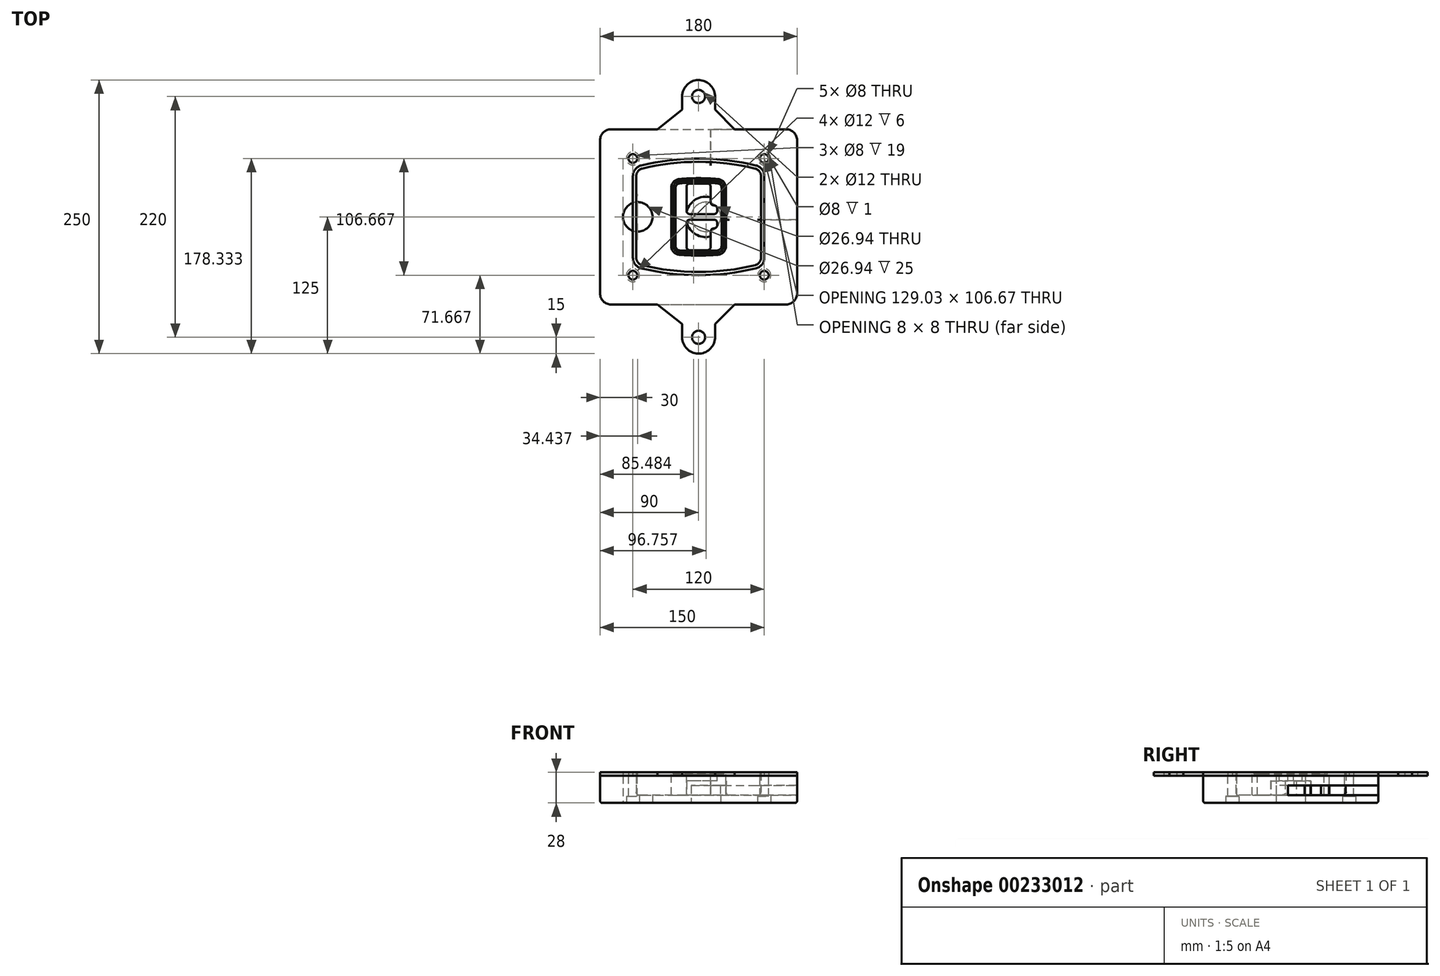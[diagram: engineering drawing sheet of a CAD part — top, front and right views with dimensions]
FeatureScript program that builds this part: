
annotation { "Feature Type Name" : "Feature", "Feature Type Description" : "" }
export const myFeature = defineFeature(function(context is Context, id is Id, definition is map)
    precondition{}
    {
        {
            var Q0;
            Q0=qCreatedBy(makeId("Top.planeOp"),FACE);
            var sketch = newSketch(context, id + "F0", { "sketchPlane" : qUnion([Q0])});
            skPoint(sketch, "E0.rect.middle", {"position": v(0, 0) * mm});
            skLineSegment(sketch, "E1.bottom", {"start": v(-80, -80) * mm, "end": v(80, -80) * mm});
            skLineSegment(sketch, "E1.top", {"start": v(-80, 80) * mm, "end": v(80, 80) * mm});
            skLineSegment(sketch, "E1.left", {"start": v(-90, -70) * mm, "end": v(-90, 70) * mm});
            skLineSegment(sketch, "E1.right", {"start": v(90, -70) * mm, "end": v(90, 70) * mm});
            skLineSegment(sketch, "E2", {"start": v(-90, 80) * mm, "end": v(90, -80) * mm, "construction": true});
            skLineSegment(sketch, "E3", {"start": v(90, 80) * mm, "end": v(-90, -80) * mm, "construction": true});
            skCircle(sketch, "E4", {"center": v(-60, 53.33) * mm, "radius": 4 * mm});
            skCircle(sketch, "E5", {"center": v(60, 53.33) * mm, "radius": 4 * mm});
            skCircle(sketch, "E6", {"center": v(60, -53.33) * mm, "radius": 4 * mm});
            skCircle(sketch, "E7", {"center": v(-60, -53.33) * mm, "radius": 4 * mm});
            skLineSegment(sketch, "E8", {"start": v(-60, 53.33) * mm, "end": v(60, 53.33) * mm, "construction": true});
            skLineSegment(sketch, "E9", {"start": v(60, 53.33) * mm, "end": v(60, -53.33) * mm, "construction": true});
            skLineSegment(sketch, "E10", {"start": v(60, -53.33) * mm, "end": v(-60, -53.33) * mm, "construction": true});
            skLineSegment(sketch, "E11", {"start": v(-60, -53.33) * mm, "end": v(-60, 53.33) * mm, "construction": true});
            skLineSegment(sketch, "E12", {"start": v(-60, 37.3) * mm, "end": v(-60, -37.3) * mm});
            skLineSegment(sketch, "E13", {"start": v(60, 37.3) * mm, "end": v(60, -37.3) * mm});
            skArc(sketch, "E14", {"start": v(52.38, 47.01) * mm, "mid": v(0, 53.33) * mm, "end": v(-52.38, 47.01) * mm});
            skArc(sketch, "E15", {"start": v(-52.38, -47.01) * mm, "mid": v(0, -53.33) * mm, "end": v(52.38, -47.01) * mm});
            skLineSegment(sketch, "E16", {"start": v(-60, 0) * mm, "end": v(60, 0) * mm, "construction": true});
            skPoint(sketch, "E17.visualSharp", {"position": v(-60, -45) * mm});
            skArc(sketch, "E17.filletArc", {"start": v(-60, -37.3) * mm, "mid": v(-57.87, -43.47) * mm, "end": v(-52.38, -47.01) * mm});
            skPoint(sketch, "E18.visualSharp", {"position": v(-60, 45) * mm});
            skArc(sketch, "E18.filletArc", {"start": v(-52.38, 47.01) * mm, "mid": v(-57.87, 43.47) * mm, "end": v(-60, 37.3) * mm});
            skPoint(sketch, "E19.visualSharp", {"position": v(60, 45) * mm});
            skArc(sketch, "E19.filletArc", {"start": v(60, 37.3) * mm, "mid": v(57.87, 43.47) * mm, "end": v(52.38, 47.01) * mm});
            skPoint(sketch, "E20.visualSharp", {"position": v(60, -45) * mm});
            skArc(sketch, "E20.filletArc", {"start": v(52.38, -47.01) * mm, "mid": v(57.87, -43.47) * mm, "end": v(60, -37.3) * mm});
            skPoint(sketch, "E21.visualSharp", {"position": v(-90, 80) * mm});
            skArc(sketch, "E21.filletArc", {"start": v(-80, 80) * mm, "mid": v(-87.07, 77.07) * mm, "end": v(-90, 70) * mm});
            skPoint(sketch, "E22.visualSharp", {"position": v(90, 80) * mm});
            skArc(sketch, "E22.filletArc", {"start": v(90, 70) * mm, "mid": v(87.07, 77.07) * mm, "end": v(80, 80) * mm});
            skPoint(sketch, "E23.visualSharp", {"position": v(90, -80) * mm});
            skArc(sketch, "E23.filletArc", {"start": v(80, -80) * mm, "mid": v(87.07, -77.07) * mm, "end": v(90, -70) * mm});
            skPoint(sketch, "E24.visualSharp", {"position": v(-90, -80) * mm});
            skArc(sketch, "E24.filletArc", {"start": v(-90, -70) * mm, "mid": v(-87.07, -77.07) * mm, "end": v(-80, -80) * mm});
            skArc(sketch, "E25.0", {"start": v(57, 37.3) * mm, "mid": v(55.5, 41.62) * mm, "end": v(51.67, 44.1) * mm});
            skLineSegment(sketch, "E25.1", {"start": v(57, 37.3) * mm, "end": v(57, -37.3) * mm});
            skArc(sketch, "E25.2", {"start": v(51.67, -44.1) * mm, "mid": v(55.5, -41.62) * mm, "end": v(57, -37.3) * mm});
            skArc(sketch, "E25.3", {"start": v(-51.67, -44.1) * mm, "mid": v(0, -50.33) * mm, "end": v(51.67, -44.1) * mm});
            skArc(sketch, "E25.4", {"start": v(-57, -37.3) * mm, "mid": v(-55.5, -41.62) * mm, "end": v(-51.67, -44.1) * mm});
            skArc(sketch, "E25.5", {"start": v(51.67, 44.1) * mm, "mid": v(0, 50.33) * mm, "end": v(-51.67, 44.1) * mm});
            skLineSegment(sketch, "E25.6", {"start": v(-57, 37.3) * mm, "end": v(-57, -37.3) * mm});
            skArc(sketch, "E25.7", {"start": v(-51.67, 44.1) * mm, "mid": v(-55.5, 41.62) * mm, "end": v(-57, 37.3) * mm});
            skArc(sketch, "E26.0", {"start": v(-53.33, 50.9) * mm, "mid": v(-61.01, 45.94) * mm, "end": v(-64, 37.3) * mm});
            skArc(sketch, "E26.1", {"start": v(53.33, 50.9) * mm, "mid": v(0, 57.33) * mm, "end": v(-53.33, 50.9) * mm});
            skArc(sketch, "E26.2", {"start": v(64, 37.3) * mm, "mid": v(61.01, 45.94) * mm, "end": v(53.33, 50.9) * mm});
            skLineSegment(sketch, "E26.3", {"start": v(64, 37.3) * mm, "end": v(64, -37.3) * mm});
            skArc(sketch, "E26.4", {"start": v(53.33, -50.9) * mm, "mid": v(61.01, -45.94) * mm, "end": v(64, -37.3) * mm});
            skLineSegment(sketch, "E26.5", {"start": v(-64, 37.3) * mm, "end": v(-64, -37.3) * mm});
            skArc(sketch, "E26.6", {"start": v(-53.33, -50.9) * mm, "mid": v(0, -57.33) * mm, "end": v(53.33, -50.9) * mm});
            skArc(sketch, "E26.7", {"start": v(-64, -37.3) * mm, "mid": v(-61.01, -45.94) * mm, "end": v(-53.33, -50.9) * mm});
            skSolve(sketch);
        }
        {
            var Q0;
            Q0=makeQuery(id+"F0.imprint","IMPRINT",FACE,{"disambiguationData":[TD([[makeQuery(id+"F0.imprint","IMPRINT",EDGE,{"derivedFrom":sQuery(id+"F0.wireOp",EDGE,"E1.bottom")}),1.0]])]});
            var Q1;
            Q1=makeQuery(id+"F0.imprint","IMPRINT",FACE,{"disambiguationData":[TD([[makeQuery(id+"F0.imprint","IMPRINT",EDGE,{"derivedFrom":sQuery(id+"F0.wireOp",EDGE,"E12")}),1.0]])]});
            var Q2;
            Q2=makeQuery(id+"F0.imprint","IMPRINT",FACE,{"disambiguationData":[TD([[makeQuery(id+"F0.imprint","IMPRINT",EDGE,{"derivedFrom":sQuery(id+"F0.wireOp",EDGE,"E25.0")}),1.0]])]});
            var Q3;
            Q3=makeQuery(id+"F0.imprint","IMPRINT",FACE,{"disambiguationData":[TD([[makeQuery(id+"F0.imprint","IMPRINT",EDGE,{"derivedFrom":sQuery(id+"F0.wireOp",EDGE,"E12")}),-1.0]])]});
            extrude(context, id + "F1", {"entities" : qUnion([Q0, Q1, Q2, Q3]), "oppositeDirection" : true, "depth" : 25 * mm});
        }
        {
            var Q0;
            Q0=makeQuery(id+"F0.imprint","IMPRINT",FACE,{"disambiguationData":[TD([[makeQuery(id+"F0.imprint","IMPRINT",EDGE,{"derivedFrom":sQuery(id+"F0.wireOp",EDGE,"E12")}),1.0]])]});
            extrude(context, id + "F2", {"entities" : qUnion([Q0]), "operationType" : NewBodyOperationType.ADD, "depth" : 3 * mm});
        }
        {
            var Q0;
            Q0=makeQuery(id+"F0.imprint","IMPRINT",FACE,{"disambiguationData":[TD([[makeQuery(id+"F0.imprint","IMPRINT",EDGE,{"derivedFrom":sQuery(id+"F0.wireOp",EDGE,"E25.0")}),1.0]])]});
            extrude(context, id + "F3", {"entities" : qUnion([Q0]), "operationType" : NewBodyOperationType.REMOVE, "oppositeDirection" : true, "depth" : 18 * mm});
        }
        {
            var Q0;
            Q0=makeQuery(id+"F2.opExtrude","CAP_FACE",FACE,{"disambiguationData":[OSD([sQuery(id+"F0.wireOp",EDGE,"E12"),sQuery(id+"F0.wireOp",EDGE,"E13"),sQuery(id+"F0.wireOp",EDGE,"E14"),sQuery(id+"F0.wireOp",EDGE,"E15"),sQuery(id+"F0.wireOp",EDGE,"E17.filletArc"),sQuery(id+"F0.wireOp",EDGE,"E18.filletArc"),sQuery(id+"F0.wireOp",EDGE,"E19.filletArc"),sQuery(id+"F0.wireOp",EDGE,"E20.filletArc"),sQuery(id+"F0.wireOp",EDGE,"E25.0"),sQuery(id+"F0.wireOp",EDGE,"E25.1"),sQuery(id+"F0.wireOp",EDGE,"E25.2"),sQuery(id+"F0.wireOp",EDGE,"E25.3"),sQuery(id+"F0.wireOp",EDGE,"E25.4"),sQuery(id+"F0.wireOp",EDGE,"E25.5"),sQuery(id+"F0.wireOp",EDGE,"E25.6"),sQuery(id+"F0.wireOp",EDGE,"E25.7")])],"isStart":false});
            var sketch = newSketch(context, id + "F4", { "sketchPlane" : qUnion([Q0])});
            skArc(sketch, "E27.0", {"start": v(-17.7, -34.56) * mm, "mid": v(0, -35.33) * mm, "end": v(17.7, -34.56) * mm});
            skArc(sketch, "E28.0", {"start": v(17.7, 34.56) * mm, "mid": v(0, 35.33) * mm, "end": v(-17.7, 34.56) * mm});
            skLineSegment(sketch, "E29", {"start": v(-25, 26.59) * mm, "end": v(-25, -26.59) * mm});
            skLineSegment(sketch, "E30", {"start": v(25, 26.59) * mm, "end": v(25, -26.59) * mm});
            skLineSegment(sketch, "E31", {"start": v(-25, 33.78) * mm, "end": v(25, 33.78) * mm, "construction": true});
            skLineSegment(sketch, "E32", {"start": v(-25, -33.78) * mm, "end": v(25, -33.78) * mm, "construction": true});
            skPoint(sketch, "E33.visualSharp", {"position": v(-25, 33.78) * mm});
            skArc(sketch, "E33.filletArc", {"start": v(-17.7, 34.56) * mm, "mid": v(-22.9, 32) * mm, "end": v(-25, 26.59) * mm});
            skPoint(sketch, "E34.visualSharp", {"position": v(25, 33.78) * mm});
            skArc(sketch, "E34.filletArc", {"start": v(25, 26.59) * mm, "mid": v(22.9, 32) * mm, "end": v(17.7, 34.56) * mm});
            skPoint(sketch, "E35.visualSharp", {"position": v(25, -33.78) * mm});
            skArc(sketch, "E35.filletArc", {"start": v(17.7, -34.56) * mm, "mid": v(22.9, -32) * mm, "end": v(25, -26.59) * mm});
            skPoint(sketch, "E36.visualSharp", {"position": v(-25, -33.78) * mm});
            skArc(sketch, "E36.filletArc", {"start": v(-25, -26.59) * mm, "mid": v(-22.9, -32) * mm, "end": v(-17.7, -34.56) * mm});
            skArc(sketch, "E37.0", {"start": v(51.67, 44.1) * mm, "mid": v(0, 50.33) * mm, "end": v(-51.67, 44.1) * mm});
            skArc(sketch, "E37.1", {"start": v(-51.67, 44.1) * mm, "mid": v(-55.5, 41.62) * mm, "end": v(-57, 37.3) * mm});
            skLineSegment(sketch, "E37.2", {"start": v(-57, 37.3) * mm, "end": v(-57, -37.3) * mm});
            skArc(sketch, "E37.3", {"start": v(-57, -37.3) * mm, "mid": v(-55.5, -41.62) * mm, "end": v(-51.67, -44.1) * mm});
            skArc(sketch, "E37.4", {"start": v(-51.67, -44.1) * mm, "mid": v(0, -50.33) * mm, "end": v(51.67, -44.1) * mm});
            skArc(sketch, "E37.5", {"start": v(51.67, -44.1) * mm, "mid": v(55.5, -41.62) * mm, "end": v(57, -37.3) * mm});
            skLineSegment(sketch, "E37.6", {"start": v(57, 37.3) * mm, "end": v(57, -37.3) * mm});
            skArc(sketch, "E37.7", {"start": v(57, 37.3) * mm, "mid": v(55.5, 41.62) * mm, "end": v(51.67, 44.1) * mm});
            skLineSegment(sketch, "E38.0", {"start": v(23, 26.59) * mm, "end": v(23, -26.59) * mm});
            skArc(sketch, "E38.1", {"start": v(17.53, -32.56) * mm, "mid": v(21.42, -30.64) * mm, "end": v(23, -26.59) * mm});
            skArc(sketch, "E38.2", {"start": v(-17.53, -32.56) * mm, "mid": v(0, -33.33) * mm, "end": v(17.53, -32.56) * mm});
            skArc(sketch, "E38.3", {"start": v(-23, -26.59) * mm, "mid": v(-21.42, -30.64) * mm, "end": v(-17.53, -32.56) * mm});
            skLineSegment(sketch, "E38.4", {"start": v(-23, 26.59) * mm, "end": v(-23, -26.59) * mm});
            skArc(sketch, "E38.5", {"start": v(23, 26.59) * mm, "mid": v(21.42, 30.64) * mm, "end": v(17.53, 32.56) * mm});
            skArc(sketch, "E38.6", {"start": v(-17.53, 32.56) * mm, "mid": v(-21.42, 30.64) * mm, "end": v(-23, 26.59) * mm});
            skArc(sketch, "E38.7", {"start": v(17.53, 32.56) * mm, "mid": v(0, 33.33) * mm, "end": v(-17.53, 32.56) * mm});
            skArc(sketch, "E39.0", {"start": v(21, 26.59) * mm, "mid": v(19.95, 29.29) * mm, "end": v(17.35, 30.57) * mm});
            skLineSegment(sketch, "E39.1", {"start": v(21, 26.59) * mm, "end": v(21, -26.59) * mm});
            skArc(sketch, "E39.2", {"start": v(17.35, -30.57) * mm, "mid": v(19.95, -29.29) * mm, "end": v(21, -26.59) * mm});
            skArc(sketch, "E39.3", {"start": v(-17.35, -30.57) * mm, "mid": v(0, -31.33) * mm, "end": v(17.35, -30.57) * mm});
            skArc(sketch, "E39.4", {"start": v(-21, -26.59) * mm, "mid": v(-19.95, -29.29) * mm, "end": v(-17.35, -30.57) * mm});
            skArc(sketch, "E39.5", {"start": v(17.35, 30.57) * mm, "mid": v(0, 31.33) * mm, "end": v(-17.35, 30.57) * mm});
            skLineSegment(sketch, "E39.6", {"start": v(-21, 26.59) * mm, "end": v(-21, -26.59) * mm});
            skArc(sketch, "E39.7", {"start": v(-17.35, 30.57) * mm, "mid": v(-19.95, 29.29) * mm, "end": v(-21, 26.59) * mm});
            skLineSegment(sketch, "E40", {"start": v(-25, 0) * mm, "end": v(25, 0) * mm, "construction": true});
            skLineSegment(sketch, "E41", {"start": v(-11, 5.5) * mm, "end": v(-11, 27.5) * mm});
            skLineSegment(sketch, "E42", {"start": v(-8, 30.5) * mm, "end": v(8, 30.5) * mm});
            skLineSegment(sketch, "E43", {"start": v(11, 27.5) * mm, "end": v(11, 13.5) * mm});
            skLineSegment(sketch, "E44", {"start": v(14, 10.5) * mm, "end": v(14, 10.5) * mm});
            skLineSegment(sketch, "E45", {"start": v(17, 7.5) * mm, "end": v(17, 5.5) * mm});
            skLineSegment(sketch, "E46", {"start": v(14, 2.5) * mm, "end": v(-8, 2.5) * mm});
            skPoint(sketch, "E47.visualSharp", {"position": v(-11, 30.5) * mm});
            skArc(sketch, "E47.filletArc", {"start": v(-8, 30.5) * mm, "mid": v(-10.12, 29.62) * mm, "end": v(-11, 27.5) * mm});
            skPoint(sketch, "E48.visualSharp", {"position": v(11, 30.5) * mm});
            skArc(sketch, "E48.filletArc", {"start": v(11, 27.5) * mm, "mid": v(10.12, 29.62) * mm, "end": v(8, 30.5) * mm});
            skPoint(sketch, "E49.visualSharp", {"position": v(11, 10.5) * mm});
            skArc(sketch, "E49.filletArc", {"start": v(11, 13.5) * mm, "mid": v(11.88, 11.38) * mm, "end": v(14, 10.5) * mm});
            skPoint(sketch, "E50.visualSharp", {"position": v(17, 10.5) * mm});
            skArc(sketch, "E50.filletArc", {"start": v(17, 7.5) * mm, "mid": v(16.12, 9.62) * mm, "end": v(14, 10.5) * mm});
            skPoint(sketch, "E51.visualSharp", {"position": v(17, 2.5) * mm});
            skArc(sketch, "E51.filletArc", {"start": v(14, 2.5) * mm, "mid": v(16.12, 3.38) * mm, "end": v(17, 5.5) * mm});
            skPoint(sketch, "E52.visualSharp", {"position": v(-11, 2.5) * mm});
            skArc(sketch, "E52.filletArc", {"start": v(-11, 5.5) * mm, "mid": v(-10.12, 3.38) * mm, "end": v(-8, 2.5) * mm});
            skLineSegment(sketch, "E53.0.MirrorCS", {"start": v(14, -2.5) * mm, "end": v(-8, -2.5) * mm});
            skArc(sketch, "E54.0.MirrorCS", {"start": v(-11, -5.5) * mm, "mid": v(-10.12, -3.38) * mm, "end": v(-8, -2.5) * mm});
            skLineSegment(sketch, "E55.0.MirrorCS", {"start": v(-11, -5.5) * mm, "end": v(-11, -27.5) * mm});
            skArc(sketch, "E56.0.MirrorCS", {"start": v(-8, -30.5) * mm, "mid": v(-10.12, -29.62) * mm, "end": v(-11, -27.5) * mm});
            skLineSegment(sketch, "E57.0.MirrorCS", {"start": v(-8, -30.5) * mm, "end": v(8, -30.5) * mm});
            skArc(sketch, "E58.0.MirrorCS", {"start": v(11, -27.5) * mm, "mid": v(10.12, -29.62) * mm, "end": v(8, -30.5) * mm});
            skLineSegment(sketch, "E59.0.MirrorCS", {"start": v(11, -27.5) * mm, "end": v(11, -13.5) * mm});
            skArc(sketch, "E60.0.MirrorCS", {"start": v(11, -13.5) * mm, "mid": v(11.88, -11.38) * mm, "end": v(14, -10.5) * mm});
            skArc(sketch, "E61.0.MirrorCS", {"start": v(17, -7.5) * mm, "mid": v(16.12, -9.62) * mm, "end": v(14, -10.5) * mm});
            skLineSegment(sketch, "E62.0.MirrorCS", {"start": v(17, -7.5) * mm, "end": v(17, -5.5) * mm});
            skArc(sketch, "E63.0.MirrorCS", {"start": v(14, -2.5) * mm, "mid": v(16.12, -3.38) * mm, "end": v(17, -5.5) * mm});
            skSolve(sketch);
        }
        {
            var Q0;
            Q0=makeQuery(id+"F4.imprint","IMPRINT",FACE,{"disambiguationData":[TD([[makeQuery(id+"F4.imprint","IMPRINT",EDGE,{"derivedFrom":sQuery(id+"F4.wireOp",EDGE,"E27.0")}),1.0]])]});
            var Q1;
            Q1=makeQuery(id+"F4.imprint","IMPRINT",FACE,{"disambiguationData":[TD([[makeQuery(id+"F4.imprint","IMPRINT",EDGE,{"derivedFrom":sQuery(id+"F4.wireOp",EDGE,"E38.0")}),-1.0]])]});
            var Q2;
            Q2=makeQuery(id+"F4.imprint","IMPRINT",FACE,{"disambiguationData":[TD([[makeQuery(id+"F4.imprint","IMPRINT",EDGE,{"derivedFrom":sQuery(id+"F4.wireOp",EDGE,"E39.0")}),1.0]])]});
            extrude(context, id + "F5", {"entities" : qUnion([Q0, Q1, Q2]), "operationType" : NewBodyOperationType.ADD, "endBound" : BoundingType.UP_TO_NEXT, "oppositeDirection" : true, "depth" : 25 * mm});
        }
        {
            var Q0;
            Q0=makeQuery(id+"F4.imprint","IMPRINT",FACE,{"disambiguationData":[TD([[makeQuery(id+"F4.imprint","IMPRINT",EDGE,{"derivedFrom":sQuery(id+"F4.wireOp",EDGE,"E38.0")}),-1.0]])]});
            extrude(context, id + "F6", {"entities" : qUnion([Q0]), "operationType" : NewBodyOperationType.REMOVE, "oppositeDirection" : true, "depth" : 2 * mm});
        }
        {
            var Q0;
            Q0=makeQuery(id+"F1.opExtrude","CAP_FACE",FACE,{"disambiguationData":[OSD([sQuery(id+"F0.wireOp",EDGE,"E1.bottom"),sQuery(id+"F0.wireOp",EDGE,"E1.top"),sQuery(id+"F0.wireOp",EDGE,"E1.left"),sQuery(id+"F0.wireOp",EDGE,"E1.right"),sQuery(id+"F0.wireOp",EDGE,"E4"),sQuery(id+"F0.wireOp",EDGE,"E5"),sQuery(id+"F0.wireOp",EDGE,"E6"),sQuery(id+"F0.wireOp",EDGE,"E7"),sQuery(id+"F0.wireOp",EDGE,"E21.filletArc"),sQuery(id+"F0.wireOp",EDGE,"E22.filletArc"),sQuery(id+"F0.wireOp",EDGE,"E23.filletArc"),sQuery(id+"F0.wireOp",EDGE,"E24.filletArc")])],"isStart":false});
            var sketch = newSketch(context, id + "F7", { "sketchPlane" : qUnion([Q0])});
            skCircle(sketch, "E64", {"center": v(6.76, 0) * mm, "radius": 13.47 * mm});
            skCircle(sketch, "E65", {"center": v(-55.56, 0) * mm, "radius": 13.47 * mm});
            skLineSegment(sketch, "E66", {"start": v(90, 0) * mm, "end": v(-90, 0) * mm});
            skCircle(sketch, "E67", {"center": v(6.76, 0) * mm, "radius": 18.47 * mm});
            skCircle(sketch, "E68", {"center": v(60, -53.33) * mm, "radius": 6 * mm});
            skCircle(sketch, "E69", {"center": v(-60, -53.33) * mm, "radius": 6 * mm});
            skCircle(sketch, "E70", {"center": v(-60, 53.33) * mm, "radius": 6 * mm});
            skCircle(sketch, "E71", {"center": v(60, 53.33) * mm, "radius": 6 * mm});
            skSolve(sketch);
        }
        {
            var Q0;
            {var subQ1=sQuery(id+"F7.wireOp",EDGE,"E66");var subQ4=sQuery(id+"F7.wireOp",EDGE,"E64");var subQ6=makeQuery(id+"F7.imprint","INTERSECT",VERTEX,{"disambiguationData":[OD(0.0)],"derivedFrom":[subQ4,subQ1]});Q0=makeQuery(id+"F7.imprint","IMPRINT",FACE,{"disambiguationData":[TD([[makeQuery(id+"F7.imprint","IMPRINT",EDGE,{"disambiguationData":[TD([[subQ6,-1.0]])],"derivedFrom":subQ4}),-1.0]])]});}
            var Q1;
            {var subQ0=sQuery(id+"F7.wireOp",EDGE,"E66");var subQ1=sQuery(id+"F7.wireOp",EDGE,"E64");var subQ3=makeQuery(id+"F7.imprint","INTERSECT",VERTEX,{"disambiguationData":[OD(0.0)],"derivedFrom":[subQ1,subQ0]});Q1=makeQuery(id+"F7.imprint","IMPRINT",FACE,{"disambiguationData":[TD([[makeQuery(id+"F7.imprint","IMPRINT",EDGE,{"disambiguationData":[TD([[subQ3,-1.0]])],"derivedFrom":subQ1}),1.0]])]});}
            var Q2;
            {var subQ0=sQuery(id+"F7.wireOp",EDGE,"E66");var subQ1=sQuery(id+"F7.wireOp",EDGE,"E64");var subQ3=makeQuery(id+"F7.imprint","INTERSECT",VERTEX,{"disambiguationData":[OD(0.0)],"derivedFrom":[subQ1,subQ0]});Q2=makeQuery(id+"F7.imprint","IMPRINT",FACE,{"disambiguationData":[TD([[makeQuery(id+"F7.imprint","IMPRINT",EDGE,{"disambiguationData":[TD([[subQ3,1.0]])],"derivedFrom":subQ1}),1.0]])]});}
            var Q3;
            {var subQ1=sQuery(id+"F7.wireOp",EDGE,"E66");var subQ4=sQuery(id+"F7.wireOp",EDGE,"E64");var subQ6=makeQuery(id+"F7.imprint","INTERSECT",VERTEX,{"disambiguationData":[OD(0.0)],"derivedFrom":[subQ4,subQ1]});Q3=makeQuery(id+"F7.imprint","IMPRINT",FACE,{"disambiguationData":[TD([[makeQuery(id+"F7.imprint","IMPRINT",EDGE,{"disambiguationData":[TD([[subQ6,1.0]])],"derivedFrom":subQ4}),-1.0]])]});}
            extrude(context, id + "F8", {"entities" : qUnion([Q0, Q1, Q2, Q3]), "operationType" : NewBodyOperationType.ADD, "oppositeDirection" : true, "depth" : 20 * mm});
        }
        {
            var Q0;
            {var subQ0=sQuery(id+"F7.wireOp",EDGE,"E66");var subQ1=sQuery(id+"F7.wireOp",EDGE,"E64");var subQ3=makeQuery(id+"F7.imprint","INTERSECT",VERTEX,{"disambiguationData":[OD(0.0)],"derivedFrom":[subQ1,subQ0]});Q0=makeQuery(id+"F7.imprint","IMPRINT",FACE,{"disambiguationData":[TD([[makeQuery(id+"F7.imprint","IMPRINT",EDGE,{"disambiguationData":[TD([[subQ3,-1.0]])],"derivedFrom":subQ1}),1.0]])]});}
            var Q1;
            {var subQ0=sQuery(id+"F7.wireOp",EDGE,"E66");var subQ1=sQuery(id+"F7.wireOp",EDGE,"E64");var subQ3=makeQuery(id+"F7.imprint","INTERSECT",VERTEX,{"disambiguationData":[OD(0.0)],"derivedFrom":[subQ1,subQ0]});Q1=makeQuery(id+"F7.imprint","IMPRINT",FACE,{"disambiguationData":[TD([[makeQuery(id+"F7.imprint","IMPRINT",EDGE,{"disambiguationData":[TD([[subQ3,1.0]])],"derivedFrom":subQ1}),1.0]])]});}
            extrude(context, id + "F9", {"entities" : qUnion([Q0, Q1]), "operationType" : NewBodyOperationType.REMOVE, "oppositeDirection" : true, "depth" : 16 * mm});
        }
        {
            var Q0;
            {var subQ0=sQuery(id+"F7.wireOp",EDGE,"E66");var subQ1=sQuery(id+"F7.wireOp",EDGE,"E65");var subQ3=makeQuery(id+"F7.imprint","INTERSECT",VERTEX,{"disambiguationData":[OD(0.0)],"derivedFrom":[subQ1,subQ0]});Q0=makeQuery(id+"F7.imprint","IMPRINT",FACE,{"disambiguationData":[TD([[makeQuery(id+"F7.imprint","IMPRINT",EDGE,{"disambiguationData":[TD([[subQ3,-1.0]])],"derivedFrom":subQ1}),1.0]])]});}
            var Q1;
            {var subQ0=sQuery(id+"F7.wireOp",EDGE,"E66");var subQ1=sQuery(id+"F7.wireOp",EDGE,"E65");var subQ3=makeQuery(id+"F7.imprint","INTERSECT",VERTEX,{"disambiguationData":[OD(0.0)],"derivedFrom":[subQ1,subQ0]});Q1=makeQuery(id+"F7.imprint","IMPRINT",FACE,{"disambiguationData":[TD([[makeQuery(id+"F7.imprint","IMPRINT",EDGE,{"disambiguationData":[TD([[subQ3,1.0]])],"derivedFrom":subQ1}),1.0]])]});}
            extrude(context, id + "F10", {"entities" : qUnion([Q0, Q1]), "operationType" : NewBodyOperationType.REMOVE, "oppositeDirection" : true, "depth" : 25 * mm});
        }
        {
            var Q0;
            Q0=makeQuery(id+"F7.imprint","IMPRINT",FACE,{"disambiguationData":[TD([[makeQuery(id+"F7.imprint","IMPRINT",EDGE,{"derivedFrom":sQuery(id+"F7.wireOp",EDGE,"E68")}),1.0]])]});
            var Q1;
            Q1=makeQuery(id+"F7.imprint","IMPRINT",FACE,{"disambiguationData":[TD([[makeQuery(id+"F7.imprint","IMPRINT",EDGE,{"derivedFrom":makeQuery(id+"F1.opExtrude","CAP_EDGE",EDGE,{"disambiguationData":[OSD([sQuery(id+"F0.wireOp",EDGE,"E5")])],"isStart":false})}),-1.0]])]});
            var Q2;
            Q2=makeQuery(id+"F7.imprint","IMPRINT",FACE,{"disambiguationData":[TD([[makeQuery(id+"F7.imprint","IMPRINT",EDGE,{"derivedFrom":sQuery(id+"F7.wireOp",EDGE,"E69")}),1.0]])]});
            var Q3;
            Q3=makeQuery(id+"F7.imprint","IMPRINT",FACE,{"disambiguationData":[TD([[makeQuery(id+"F7.imprint","IMPRINT",EDGE,{"derivedFrom":makeQuery(id+"F1.opExtrude","CAP_EDGE",EDGE,{"disambiguationData":[OSD([sQuery(id+"F0.wireOp",EDGE,"E4")])],"isStart":false})}),-1.0]])]});
            var Q4;
            Q4=makeQuery(id+"F7.imprint","IMPRINT",FACE,{"disambiguationData":[TD([[makeQuery(id+"F7.imprint","IMPRINT",EDGE,{"derivedFrom":sQuery(id+"F7.wireOp",EDGE,"E70")}),1.0]])]});
            var Q5;
            Q5=makeQuery(id+"F7.imprint","IMPRINT",FACE,{"disambiguationData":[TD([[makeQuery(id+"F7.imprint","IMPRINT",EDGE,{"derivedFrom":makeQuery(id+"F1.opExtrude","CAP_EDGE",EDGE,{"disambiguationData":[OSD([sQuery(id+"F0.wireOp",EDGE,"E7")])],"isStart":false})}),-1.0]])]});
            var Q6;
            Q6=makeQuery(id+"F7.imprint","IMPRINT",FACE,{"disambiguationData":[TD([[makeQuery(id+"F7.imprint","IMPRINT",EDGE,{"derivedFrom":sQuery(id+"F7.wireOp",EDGE,"E71")}),1.0]])]});
            var Q7;
            Q7=makeQuery(id+"F7.imprint","IMPRINT",FACE,{"disambiguationData":[TD([[makeQuery(id+"F7.imprint","IMPRINT",EDGE,{"derivedFrom":makeQuery(id+"F1.opExtrude","CAP_EDGE",EDGE,{"disambiguationData":[OSD([sQuery(id+"F0.wireOp",EDGE,"E6")])],"isStart":false})}),-1.0]])]});
            extrude(context, id + "F11", {"entities" : qUnion([Q0, Q1, Q2, Q3, Q4, Q5, Q6, Q7]), "operationType" : NewBodyOperationType.REMOVE, "oppositeDirection" : true, "depth" : 6 * mm});
        }
        {
            var Q0;
            Q0=makeQuery(id+"F9.boolean.opBoolean","COPY",FACE,{"derivedFrom":makeQuery(id+"F9.opExtrude","CAP_FACE",FACE,{"disambiguationData":[OSD([sQuery(id+"F7.wireOp",EDGE,"E64")])],"isStart":false})});
            var sketch = newSketch(context, id + "F12", { "sketchPlane" : qUnion([Q0])});
            skArc(sketch, "E72.0", {"start": v(11, -88.19) * mm, "mid": v(97.1, -83.6) * mm, "end": v(92.5, 2.5) * mm});
            skLineSegment(sketch, "E72.1", {"start": v(11, -17.97) * mm, "end": v(11, -17.97) * mm});
            skLineSegment(sketch, "E73", {"start": v(92.5, -105.13) * mm, "end": v(102.3, -105.13) * mm});
            skLineSegment(sketch, "E74.0", {"start": v(92.5, 2.5) * mm, "end": v(14, 2.5) * mm});
            skArc(sketch, "E74.1", {"start": v(14, 2.5) * mm, "mid": v(16.12, 3.38) * mm, "end": v(17, 5.5) * mm});
            skLineSegment(sketch, "E74.2", {"start": v(17, 7.5) * mm, "end": v(17, 5.5) * mm});
            skArc(sketch, "E74.3", {"start": v(17, 7.5) * mm, "mid": v(16.12, 9.62) * mm, "end": v(14, 10.5) * mm});
            skArc(sketch, "E74.4", {"start": v(11, 13.5) * mm, "mid": v(11.88, 11.38) * mm, "end": v(14, 10.5) * mm});
            skLineSegment(sketch, "E74.5", {"start": v(11, 13.5) * mm, "end": v(11, -88.19) * mm});
            skLineSegment(sketch, "E74.7", {"start": v(92.5, -2.5) * mm, "end": v(14, -2.5) * mm});
            skArc(sketch, "E74.8", {"start": v(14, -2.5) * mm, "mid": v(16.12, -3.38) * mm, "end": v(17, -5.5) * mm});
            skLineSegment(sketch, "E74.9", {"start": v(17, -7.5) * mm, "end": v(17, -5.5) * mm});
            skArc(sketch, "E74.10", {"start": v(17, -7.5) * mm, "mid": v(16.12, -9.62) * mm, "end": v(14, -10.5) * mm});
            skArc(sketch, "E74.11", {"start": v(11, -13.5) * mm, "mid": v(11.88, -11.38) * mm, "end": v(14, -10.5) * mm});
            skLineSegment(sketch, "E74.12", {"start": v(11, -17.97) * mm, "end": v(11, -13.5) * mm});
            skPoint(sketch, "E75.orphan", {"position": v(11, -27.5) * mm});
            skPoint(sketch, "E76.orphan", {"position": v(-8, -2.5) * mm});
            skPoint(sketch, "E77.orphan", {"position": v(-8, 2.5) * mm});
            skPoint(sketch, "E78.orphan", {"position": v(11, 27.5) * mm});
            skSolve(sketch);
        }
        {
            var Q0;
            {var subQ7=sQuery(id+"F12.wireOp",EDGE,"E72.0");var subQ14=sQuery(id+"F12.wireOp",EDGE,"E72.1");var subQ16=sQuery(id+"F12.wireOp",EDGE,"E74.1");var subQ18=sQuery(id+"F12.wireOp",EDGE,"E74.8");Q0=qUnion([makeQuery(id+"F12.imprint","IMPRINT",FACE,{"disambiguationData":[TD([[makeQuery(id+"F12.imprint","IMPRINT",EDGE,{"derivedFrom":subQ7}),1.0]])]}),makeQuery(id+"F12.imprint","IMPRINT",FACE,{"disambiguationData":[TD([[makeQuery(id+"F12.imprint","IMPRINT",EDGE,{"derivedFrom":subQ14}),1.0]])]}),makeQuery(id+"F12.imprint","IMPRINT",FACE,{"disambiguationData":[TD([[makeQuery(id+"F12.imprint","IMPRINT",EDGE,{"derivedFrom":subQ16}),1.0]])]}),makeQuery(id+"F12.imprint","IMPRINT",FACE,{"disambiguationData":[TD([[makeQuery(id+"F12.imprint","IMPRINT",EDGE,{"derivedFrom":subQ18}),-1.0]])]})]);}
            var Q1;
            Q1=makeQuery(id+"F5.boolean.opBoolean","SPLIT",FACE,{"disambiguationData":[TD([makeQuery(id+"F5.opExtrude","SWEPT_FACE",FACE,{"disambiguationData":[OSD([sQuery(id+"F4.wireOp",EDGE,"E41")])]})])],"derivedFrom":makeQuery(id+"F3.boolean.opBoolean","COPY",FACE,{"derivedFrom":makeQuery(id+"F3.opExtrude","CAP_FACE",FACE,{"disambiguationData":[OSD([sQuery(id+"F0.wireOp",EDGE,"E25.0"),sQuery(id+"F0.wireOp",EDGE,"E25.1"),sQuery(id+"F0.wireOp",EDGE,"E25.2"),sQuery(id+"F0.wireOp",EDGE,"E25.3"),sQuery(id+"F0.wireOp",EDGE,"E25.4"),sQuery(id+"F0.wireOp",EDGE,"E25.5"),sQuery(id+"F0.wireOp",EDGE,"E25.6"),sQuery(id+"F0.wireOp",EDGE,"E25.7")])],"isStart":false})})});
            extrude(context, id + "F13", {"entities" : qUnion([Q0]), "operationType" : NewBodyOperationType.REMOVE, "endBound" : BoundingType.UP_TO_SURFACE, "endBoundEntityFace" : qUnion([Q1]), "depth" : 25 * mm});
        }
        {
            var Q0;
            Q0=makeQuery(id+"F3.boolean.opBoolean","COPY",EDGE,{"derivedFrom":makeQuery(id+"F3.opExtrude","CAP_EDGE",EDGE,{"disambiguationData":[OSD([sQuery(id+"F0.wireOp",EDGE,"E25.6")])],"isStart":false})});
            var Q1;
            Q1=makeQuery(id+"F8.boolean.opBoolean","INTERSECT",EDGE,{"derivedFrom":[makeQuery(id+"F5.opExtrude","SWEPT_FACE",FACE,{"disambiguationData":[OSD([sQuery(id+"F4.wireOp",EDGE,"E30")])]}),makeQuery(id+"F8.opExtrude","CAP_FACE",FACE,{"disambiguationData":[OSD([sQuery(id+"F7.wireOp",EDGE,"E67")])],"isStart":false})]});
            var Q2;
            Q2=makeQuery(id+"F8.boolean.opBoolean","INTERSECT",EDGE,{"disambiguationData":[OD(1.0)],"derivedFrom":[makeQuery(id+"F5.opExtrude","SWEPT_FACE",FACE,{"disambiguationData":[OSD([sQuery(id+"F4.wireOp",EDGE,"E30")])]}),makeQuery(id+"F8.opExtrude","SWEPT_FACE",FACE,{"disambiguationData":[OSD([sQuery(id+"F7.wireOp",EDGE,"E67")])]})]});
            var Q3;
            {var subQ0=makeQuery(id+"F3.boolean.opBoolean","COPY",FACE,{"derivedFrom":makeQuery(id+"F3.opExtrude","CAP_FACE",FACE,{"disambiguationData":[OSD([sQuery(id+"F0.wireOp",EDGE,"E25.0"),sQuery(id+"F0.wireOp",EDGE,"E25.1"),sQuery(id+"F0.wireOp",EDGE,"E25.2"),sQuery(id+"F0.wireOp",EDGE,"E25.3"),sQuery(id+"F0.wireOp",EDGE,"E25.4"),sQuery(id+"F0.wireOp",EDGE,"E25.5"),sQuery(id+"F0.wireOp",EDGE,"E25.6"),sQuery(id+"F0.wireOp",EDGE,"E25.7")])],"isStart":false})});var subQ1=sQuery(id+"F4.wireOp",EDGE,"E30");Q3=makeQuery(id+"F8.boolean.opBoolean","SPLIT",EDGE,{"disambiguationData":[TD([makeQuery(id+"F5.opExtrude","SWEPT_FACE",FACE,{"disambiguationData":[OSD([sQuery(id+"F4.wireOp",EDGE,"E35.filletArc")])]})])],"derivedFrom":makeQuery(id+"F5.opExtrude","TWEAK_EDGE",EDGE,{"derivedFrom":[subQ0,makeQuery(id+"F4.imprint","IMPRINT",EDGE,{"derivedFrom":subQ1})]})});}
            var Q4;
            {var subQ0=sQuery(id+"F0.wireOp",EDGE,"E25.0");var subQ1=sQuery(id+"F0.wireOp",EDGE,"E25.1");var subQ2=sQuery(id+"F0.wireOp",EDGE,"E25.2");var subQ3=sQuery(id+"F0.wireOp",EDGE,"E25.3");var subQ4=sQuery(id+"F0.wireOp",EDGE,"E25.4");var subQ5=sQuery(id+"F0.wireOp",EDGE,"E25.5");var subQ6=sQuery(id+"F0.wireOp",EDGE,"E25.6");var subQ7=sQuery(id+"F0.wireOp",EDGE,"E25.7");Q4=makeQuery(id+"F8.boolean.opBoolean","INTERSECT",EDGE,{"derivedFrom":[makeQuery(id+"F5.boolean.opBoolean","SPLIT",FACE,{"disambiguationData":[TD([makeQuery(id+"F2.opExtrude","SWEPT_FACE",FACE,{"disambiguationData":[OSD([subQ0])]})])],"derivedFrom":makeQuery(id+"F3.boolean.opBoolean","COPY",FACE,{"derivedFrom":makeQuery(id+"F3.opExtrude","CAP_FACE",FACE,{"disambiguationData":[OSD([subQ0,subQ1,subQ2,subQ3,subQ4,subQ5,subQ6,subQ7])],"isStart":false})})}),makeQuery(id+"F8.opExtrude","SWEPT_FACE",FACE,{"disambiguationData":[OSD([sQuery(id+"F7.wireOp",EDGE,"E67")])]})]});}
            var Q5;
            Q5=makeQuery(id+"F8.boolean.opBoolean","INTERSECT",EDGE,{"disambiguationData":[OD(0.0)],"derivedFrom":[makeQuery(id+"F5.opExtrude","SWEPT_FACE",FACE,{"disambiguationData":[OSD([sQuery(id+"F4.wireOp",EDGE,"E30")])]}),makeQuery(id+"F8.opExtrude","SWEPT_FACE",FACE,{"disambiguationData":[OSD([sQuery(id+"F7.wireOp",EDGE,"E67")])]})]});
            fillet(context, id + "F14", {"entities" : qUnion([Q0, Q1, Q2, Q3, Q4, Q5]), "radius" : 3 * mm, "tangentPropagation" : true, "allowEdgeOverflow" : false});
        }
        {
            var Q0;
            Q0=makeQuery(id+"F1.opExtrude","CAP_EDGE",EDGE,{"disambiguationData":[OSD([sQuery(id+"F0.wireOp",EDGE,"E1.bottom")])],"isStart":false});
            fillet(context, id + "F15", {"entities" : qUnion([Q0]), "radius" : 2 * mm, "tangentPropagation" : true, "allowEdgeOverflow" : false});
        }
        {
            var Q0;
            {var subQ0=sQuery(id+"F0.wireOp",EDGE,"E22.filletArc");var subQ1=sQuery(id+"F0.wireOp",EDGE,"E7");var subQ2=sQuery(id+"F0.wireOp",EDGE,"E6");var subQ3=sQuery(id+"F0.wireOp",EDGE,"E5");var subQ4=sQuery(id+"F0.wireOp",EDGE,"E4");var subQ5=sQuery(id+"F0.wireOp",EDGE,"E1.bottom");var subQ6=sQuery(id+"F0.wireOp",EDGE,"E21.filletArc");var subQ7=sQuery(id+"F0.wireOp",EDGE,"E1.top");var subQ8=sQuery(id+"F0.wireOp",EDGE,"E1.left");var subQ9=sQuery(id+"F0.wireOp",EDGE,"E1.right");var subQ10=sQuery(id+"F0.wireOp",EDGE,"E23.filletArc");var subQ11=sQuery(id+"F0.wireOp",EDGE,"E24.filletArc");Q0=makeQuery(id+"F2.boolean.opBoolean","SPLIT",FACE,{"disambiguationData":[TD([makeQuery(id+"F1.opExtrude","SWEPT_FACE",FACE,{"disambiguationData":[OSD([subQ5])]})])],"derivedFrom":makeQuery(id+"F1.opExtrude","CAP_FACE",FACE,{"disambiguationData":[OSD([subQ5,subQ7,subQ8,subQ9,subQ4,subQ3,subQ2,subQ1,subQ6,subQ0,subQ10,subQ11])],"isStart":true})});}
            var sketch = newSketch(context, id + "F16", { "sketchPlane" : qUnion([Q0])});
            skLineSegment(sketch, "E79", {"start": v(-37.49, 80) * mm, "end": v(-15, 98) * mm});
            skLineSegment(sketch, "E80", {"start": v(14.97, 98) * mm, "end": v(32.97, 80) * mm});
            skLineSegment(sketch, "E81", {"start": v(-15, 98) * mm, "end": v(-15, 110) * mm});
            skLineSegment(sketch, "E82", {"start": v(14.97, 98) * mm, "end": v(14.97, 110.87) * mm});
            skCircle(sketch, "E83", {"center": v(0, 110) * mm, "radius": 6 * mm});
            skLineSegment(sketch, "E84", {"start": v(0, 110) * mm, "end": v(0, 80) * mm, "construction": true});
            skArc(sketch, "E85", {"start": v(14.97, 110.87) * mm, "mid": v(-0.43, 125) * mm, "end": v(-15, 110) * mm});
            skLineSegment(sketch, "E86", {"start": v(-90, 0) * mm, "end": v(90, 0) * mm, "construction": true});
            skLineSegment(sketch, "E87.MirrorCS", {"start": v(14.97, -98) * mm, "end": v(14.97, -110.87) * mm});
            skLineSegment(sketch, "E88.MirrorCS", {"start": v(-15, -98) * mm, "end": v(-15, -110) * mm});
            skLineSegment(sketch, "E89.MirrorCS", {"start": v(-37.49, -80) * mm, "end": v(-15, -98) * mm});
            skCircle(sketch, "E90.MirrorC", {"center": v(0, -110) * mm, "radius": 6 * mm});
            skLineSegment(sketch, "E91.MirrorCS", {"start": v(14.97, -98) * mm, "end": v(32.97, -80) * mm});
            skLineSegment(sketch, "E92.MirrorCS", {"start": v(0, -110) * mm, "end": v(0, -80) * mm, "construction": true});
            skArc(sketch, "E93.MirrorCS", {"start": v(14.97, -110.87) * mm, "mid": v(-0.43, -125) * mm, "end": v(-15, -110) * mm});
            skSolve(sketch);
        }
        {
            var Q0;
            {var subQ1=sQuery(id+"F16.wireOp",EDGE,"E79");Q0=makeQuery(id+"F16.imprint","IMPRINT",FACE,{"disambiguationData":[TD([[makeQuery(id+"F16.imprint","IMPRINT",EDGE,{"derivedFrom":subQ1}),-1.0]])]});}
            var Q1;
            Q1=makeQuery(id+"F16.imprint","IMPRINT",FACE,{"disambiguationData":[TD([[makeQuery(id+"F16.imprint","IMPRINT",EDGE,{"derivedFrom":sQuery(id+"F16.wireOp",EDGE,"E87.MirrorCS")}),-1.0]])]});
            var Q2;
            Q2=makeQuery(id+"F16.imprint","IMPRINT",FACE,{"disambiguationData":[TD([[makeQuery(id+"F16.imprint","IMPRINT",EDGE,{"derivedFrom":makeQuery(id+"F1.opExtrude","CAP_EDGE",EDGE,{"disambiguationData":[OSD([sQuery(id+"F0.wireOp",EDGE,"E1.left")])],"isStart":true})}),-1.0]])]});
            var Q3;
            Q3=makeQuery(id+"F2.opExtrude","CAP_FACE",FACE,{"disambiguationData":[OSD([sQuery(id+"F0.wireOp",EDGE,"E12"),sQuery(id+"F0.wireOp",EDGE,"E13"),sQuery(id+"F0.wireOp",EDGE,"E14"),sQuery(id+"F0.wireOp",EDGE,"E15"),sQuery(id+"F0.wireOp",EDGE,"E17.filletArc"),sQuery(id+"F0.wireOp",EDGE,"E18.filletArc"),sQuery(id+"F0.wireOp",EDGE,"E19.filletArc"),sQuery(id+"F0.wireOp",EDGE,"E20.filletArc"),sQuery(id+"F0.wireOp",EDGE,"E25.0"),sQuery(id+"F0.wireOp",EDGE,"E25.1"),sQuery(id+"F0.wireOp",EDGE,"E25.2"),sQuery(id+"F0.wireOp",EDGE,"E25.3"),sQuery(id+"F0.wireOp",EDGE,"E25.4"),sQuery(id+"F0.wireOp",EDGE,"E25.5"),sQuery(id+"F0.wireOp",EDGE,"E25.6"),sQuery(id+"F0.wireOp",EDGE,"E25.7")])],"isStart":false});
            extrude(context, id + "F17", {"entities" : qUnion([Q0, Q1, Q2]), "endBound" : BoundingType.UP_TO_SURFACE, "endBoundEntityFace" : qUnion([Q3]), "depth" : 25 * mm});
        }
    });
